# Revit family: Shower-Shower_Trim-KOHLER-July-K-TS98008_1
name_source: partatom
category: Plumbing Fixtures
revit_build: Autodesk Revit 2017 (Build: 20160225_1515(x64)
units: mm (PartAtom-declared; Revit-internal decimal feet)

## family parameters
Cut with Voids When Loaded = No
Host = Face
OmniClass Number = 23.31.17.00
OmniClass Title = Showers
Part Type = Normal
Room Calculation Point = No
Round Connector Dimension = Use Diameter
Shared = No

## types (3) — shared parameters
ADA Compliant = No
Assembly Code = D2010700
CW Connection = No
Cold Water Inlet = Cold Water Inlet
Date Modified = 11/11/2020
Default Elevation = 42"
Drain Included = No
Flow Rate = 2 GPM
HW Connection = Yes
Handle Clearance = 4 1/8"
Height = 6 1/2"
Hot Water Inlet = Hot Water Inlet
Length = 7 1/2"
Manufacturer = KOHLER Co.
Master Format 2014 = 22 42 23
Master Format 2014 Name = Residential Showers
Material = Premium Metal Construction
Pressure = 80.00 psi
Product Documentation Link = https://www.us.kohler.com
Product Name = July
Product Page URL = http://www.us.kohler.com
Tempered Water Inlet = Tempered Water Inlet
URL = https://www.us.kohler.com
Vent Connection = No
Waste Connection = No
Waste Water Outlet = Waste Water Outlet
WaterSense Certified = Yes
Width = 6 1/2"

## per-type parameters (varying)
| type | Description | Finish | Model | Type |
| 2.0 GPM, CP-Polished Chrome | Rite-Temp shower trim with lever handle and 2.0 gpm showerhead | Kohler-Metal-CP-Polished_Chrome | K-TS98008-4-CP | 1 |
| 2.0 GPM, G-Brushed Chrome | Rite-Temp shower trim with lever handle and 2.0 gpm showerhead | Kohler-Metal-G-Brushed_Chrome | K-TS98008-4-G | 2 |
| 1.75 GPM, CP-Polished Chrome | Rite-Temp shower trim with lever handle and 1.75 gpm showerhead | Kohler-Metal-CP-Polished_Chrome | K-TS98008-4G-CP | 3 |

## geometry (parser evidence)
native form markers: Sweep x8
no freeform markers — native parametric forms only
